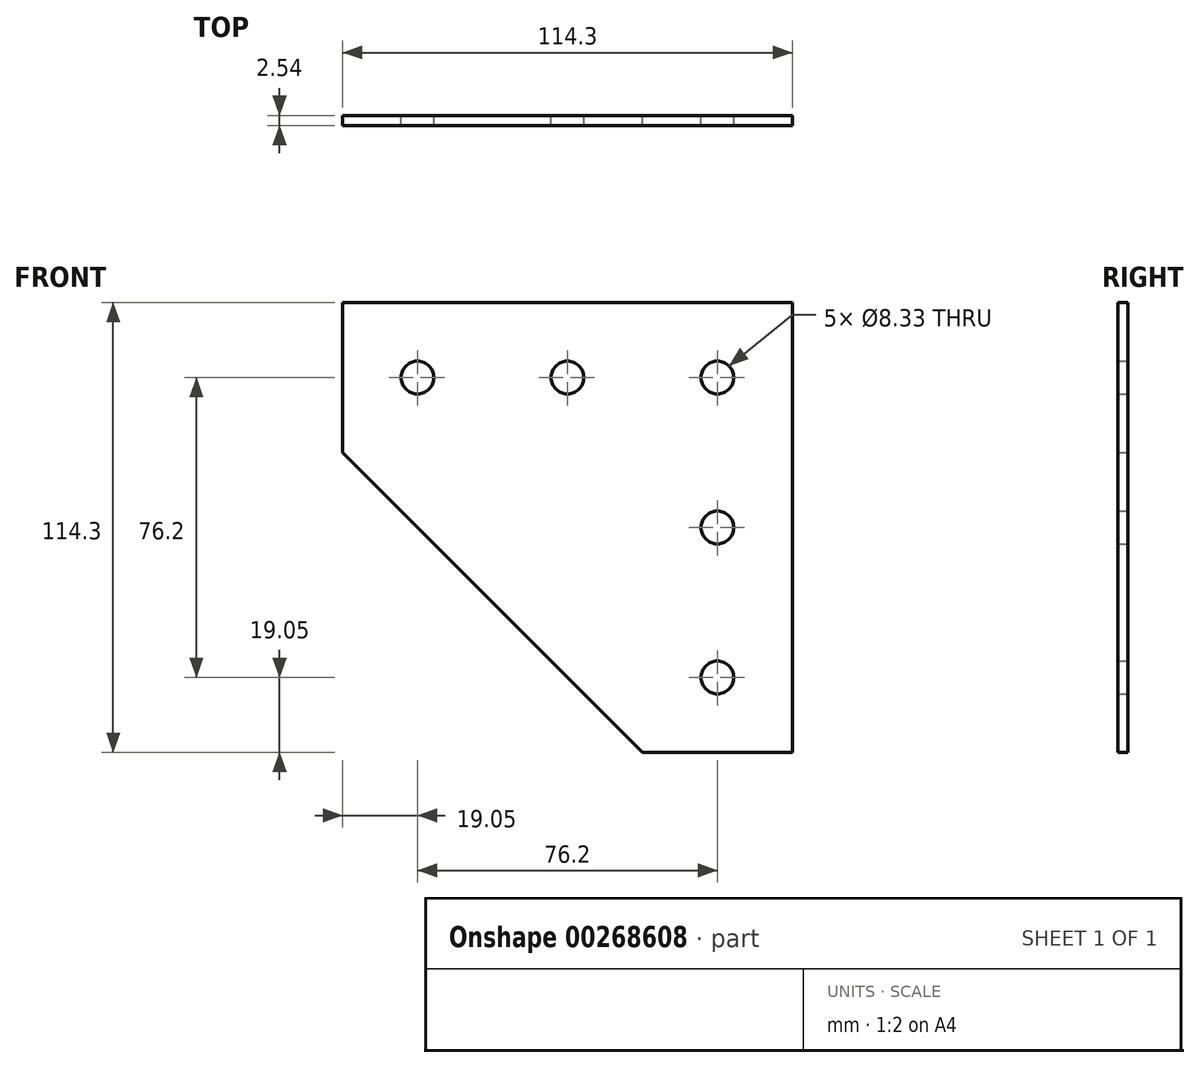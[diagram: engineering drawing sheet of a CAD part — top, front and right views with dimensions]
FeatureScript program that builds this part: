
annotation { "Feature Type Name" : "Feature", "Feature Type Description" : "" }
export const myFeature = defineFeature(function(context is Context, id is Id, definition is map)
    precondition{}
    {
        {
            var Q0;
            Q0=qCreatedBy(makeId("Front.planeOp"),FACE);
            var sketch = newSketch(context, id + "F0", { "sketchPlane" : qUnion([Q0])});
            skLineSegment(sketch, "E0.top", {"start": v(57.15, 57.15) * mm, "end": v(-57.15, 57.15) * mm});
            skLineSegment(sketch, "E0.left", {"start": v(57.15, -57.15) * mm, "end": v(57.15, 57.15) * mm});
            skPoint(sketch, "E0.middle", {"position": v(0, 0) * mm});
            skCircle(sketch, "E1", {"center": v(38.1, 38.1) * mm, "radius": 4.17 * mm});
            skLineSegment(sketch, "E2", {"start": v(-57.15, 57.15) * mm, "end": v(-57.15, 19.05) * mm});
            skLineSegment(sketch, "E3", {"start": v(57.15, -57.15) * mm, "end": v(19.05, -57.15) * mm});
            skLineSegment(sketch, "E4", {"start": v(-57.15, 19.05) * mm, "end": v(19.05, -57.15) * mm});
            skCircle(sketch, "E5.1.0.0", {"center": v(0, 38.1) * mm, "radius": 4.17 * mm});
            skCircle(sketch, "E5.2.0.0", {"center": v(-38.1, 38.1) * mm, "radius": 4.17 * mm});
            skLineSegment(sketch, "E5.direction1", {"start": v(38.1, 38.1) * mm, "end": v(0, 38.1) * mm, "construction": true});
            skCircle(sketch, "E6.0.1.0", {"center": v(38.1, 0) * mm, "radius": 4.17 * mm});
            skCircle(sketch, "E6.0.2.0", {"center": v(38.1, -38.1) * mm, "radius": 4.17 * mm});
            skLineSegment(sketch, "E6.direction1", {"start": v(38.1, 38.1) * mm, "end": v(63.5, 38.1) * mm, "construction": true});
            skLineSegment(sketch, "E6.direction2", {"start": v(38.1, 38.1) * mm, "end": v(38.1, 0) * mm, "construction": true});
            skSolve(sketch);
        }
        {
            var Q0;
            Q0=makeQuery(id+"F0.imprint","IMPRINT",FACE,{"disambiguationData":[TD([[makeQuery(id+"F0.imprint","IMPRINT",EDGE,{"derivedFrom":sQuery(id+"F0.wireOp",EDGE,"E0.top")}),1.0]])]});
            extrude(context, id + "F1", {"entities" : qUnion([Q0]), "depth" : 2.54 * mm});
        }
    });
